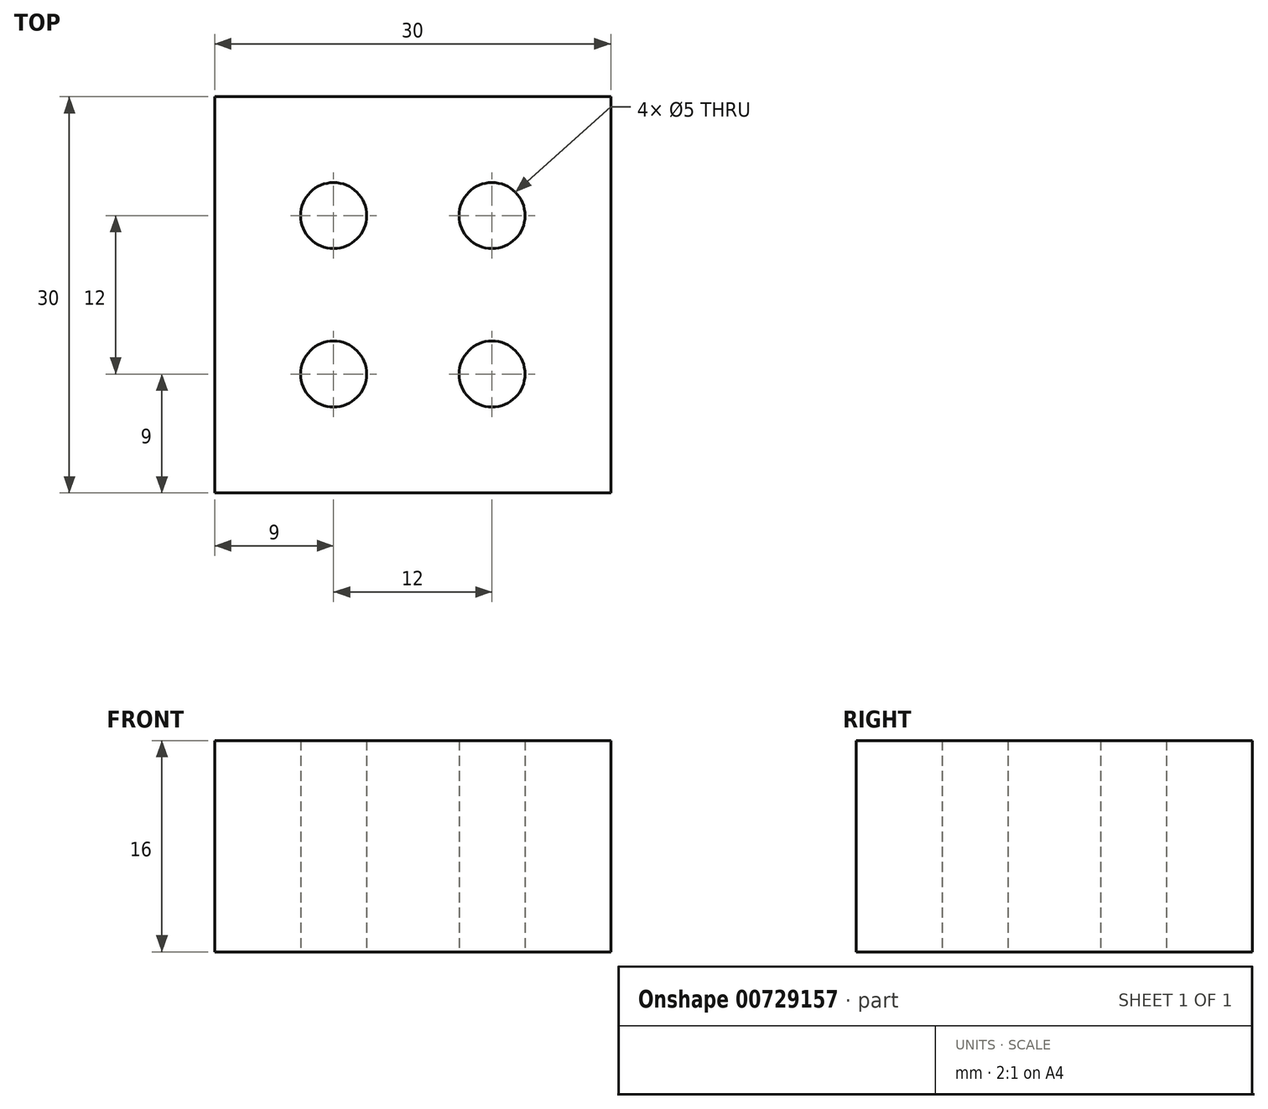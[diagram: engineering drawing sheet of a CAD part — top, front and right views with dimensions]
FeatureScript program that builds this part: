
annotation { "Feature Type Name" : "Feature", "Feature Type Description" : "" }
export const myFeature = defineFeature(function(context is Context, id is Id, definition is map)
    precondition{}
    {
        {
            var Q0;
            Q0=qCreatedBy(makeId("Top.planeOp"),FACE);
            var sketch = newSketch(context, id + "F0", { "sketchPlane" : qUnion([Q0])});
            skLineSegment(sketch, "E0.bottom", {"start": v(15, -15) * mm, "end": v(-15, -15) * mm});
            skLineSegment(sketch, "E0.top", {"start": v(15, 15) * mm, "end": v(-15, 15) * mm});
            skLineSegment(sketch, "E0.left", {"start": v(15, -15) * mm, "end": v(15, 15) * mm});
            skLineSegment(sketch, "E0.right", {"start": v(-15, -15) * mm, "end": v(-15, 15) * mm});
            skPoint(sketch, "E0.middle", {"position": v(0, 0) * mm});
            skLineSegment(sketch, "E1.bottom", {"start": v(6, 6) * mm, "end": v(-6, 6) * mm, "construction": true});
            skLineSegment(sketch, "E1.top", {"start": v(6, -6) * mm, "end": v(-6, -6) * mm, "construction": true});
            skLineSegment(sketch, "E1.left", {"start": v(6, 6) * mm, "end": v(6, -6) * mm, "construction": true});
            skLineSegment(sketch, "E1.right", {"start": v(-6, 6) * mm, "end": v(-6, -6) * mm, "construction": true});
            skSolve(sketch);
        }
        {
            var Q0;
            Q0=makeQuery(id+"F0.imprint","IMPRINT",FACE,{"disambiguationData":[TD([[makeQuery(id+"F0.imprint","IMPRINT",EDGE,{"derivedFrom":sQuery(id+"F0.wireOp",EDGE,"E0.bottom")}),-1.0]])]});
            extrude(context, id + "F1", {"entities" : qUnion([Q0]), "depth" : 16 * mm, "offsetDistance" : 25 * mm});
        }
        {
            var Q0;
            Q0=sQuery(id+"F0.wireOp",VERTEX,"E1.right.start");
            var Q1;
            Q1=sQuery(id+"F0.wireOp",VERTEX,"E1.top.start");
            var Q2;
            Q2=sQuery(id+"F0.wireOp",VERTEX,"E1.top.end");
            var Q3;
            Q3=sQuery(id+"F0.wireOp",VERTEX,"E1.left.start");
            var Q4;
            Q4=sQuery(id+"F0.wireOp",VERTEX,"1ddb5b0f-67f4-40bf-8c2f-a591401556b6.top.end");
            var Q5;
            Q5=sQuery(id+"F0.wireOp",VERTEX,"f3c1cda6-16f7-4d27-9da2-253d07f18b4f");
            var Q6;
            Q6=makeQuery(id+"F1.opExtrude","SWEPT_BODY",BODY,{"disambiguationData":[OSD([sQuery(id+"F0.wireOp",EDGE,"E0.bottom"),sQuery(id+"F0.wireOp",EDGE,"E0.top"),sQuery(id+"F0.wireOp",EDGE,"E0.left"),sQuery(id+"F0.wireOp",EDGE,"E0.right")])]});
            hole(context, id + "F2", {"style" : HoleStyle.SIMPLE, "endStyle" : HoleEndStyle.THROUGH, "oppositeDirection" : true, "holeDiameter" : 5 * mm, "majorDiameter" : 5 * mm, "isTappedThrough" : true, "tappedDepth" : 12 * mm, "tapClearance" : 3, "locations" : qUnion([Q0, Q1, Q2, Q3, Q4, Q5]), "scope" : qUnion([Q6])});
        }
    });
